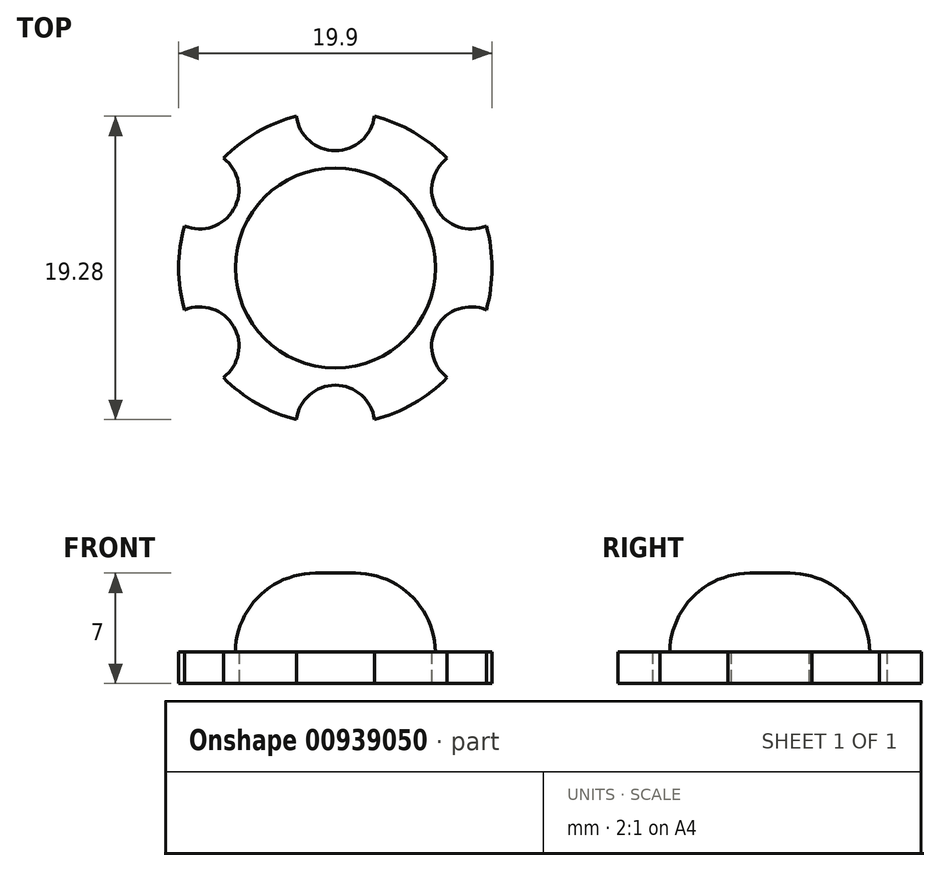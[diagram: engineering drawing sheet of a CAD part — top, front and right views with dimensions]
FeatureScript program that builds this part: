
annotation { "Feature Type Name" : "Feature", "Feature Type Description" : "" }
export const myFeature = defineFeature(function(context is Context, id is Id, definition is map)
    precondition{}
    {
        {
            var Q0;
            Q0=qCreatedBy(makeId("Top.planeOp"),FACE);
            var sketch = newSketch(context, id + "F0", { "sketchPlane" : qUnion([Q0])});
            skCircle(sketch, "E0", {"center": v(0, 0) * mm, "radius": 9.95 * mm});
            skCircle(sketch, "E1", {"center": v(0, 9.95) * mm, "radius": 2.5 * mm});
            skCircle(sketch, "E2.1.0", {"center": v(-8.62, 4.98) * mm, "radius": 2.5 * mm});
            skCircle(sketch, "E2.2.0", {"center": v(-8.62, -4.97) * mm, "radius": 2.5 * mm});
            skCircle(sketch, "E2.3.0", {"center": v(0, -9.95) * mm, "radius": 2.5 * mm});
            skCircle(sketch, "E2.4.0", {"center": v(8.62, -4.98) * mm, "radius": 2.5 * mm});
            skCircle(sketch, "E2.5.0", {"center": v(8.62, 4.98) * mm, "radius": 2.5 * mm});
            skSolve(sketch);
        }
        {
            var Q0;
            {var subQ0=sQuery(id+"F0.wireOp",EDGE,"E2.5.0");var subQ1=sQuery(id+"F0.wireOp",EDGE,"E0");var subQ11=makeQuery(id+"F0.imprint","INTERSECT",VERTEX,{"disambiguationData":[OD(0.0)],"derivedFrom":[subQ1,subQ0]});Q0=makeQuery(id+"F0.imprint","IMPRINT",FACE,{"disambiguationData":[TD([[makeQuery(id+"F0.imprint","IMPRINT",EDGE,{"disambiguationData":[TD([[subQ11,-1.0]])],"derivedFrom":subQ1}),1.0]])]});}
            extrude(context, id + "F1", {"entities" : qUnion([Q0]), "depth" : 2 * mm, "offsetDistance" : 25.4 * mm});
        }
        {
            var Q0;
            Q0=makeQuery(id+"F1.opExtrude","CAP_FACE",FACE,{"disambiguationData":[OSD([sQuery(id+"F0.wireOp",EDGE,"E0"),sQuery(id+"F0.wireOp",EDGE,"E1"),sQuery(id+"F0.wireOp",EDGE,"E2.1.0"),sQuery(id+"F0.wireOp",EDGE,"E2.2.0"),sQuery(id+"F0.wireOp",EDGE,"E2.3.0"),sQuery(id+"F0.wireOp",EDGE,"E2.4.0"),sQuery(id+"F0.wireOp",EDGE,"E2.5.0")])],"isStart":false});
            var sketch = newSketch(context, id + "F2", { "sketchPlane" : qUnion([Q0])});
            skCircle(sketch, "E3", {"center": v(0, 0) * mm, "radius": 6.35 * mm});
            skSolve(sketch);
        }
        {
            var Q0;
            Q0 = qSketchRegion(id + "F2", true);
            extrude(context, id + "F3", {"entities" : qUnion([Q0]), "operationType" : NewBodyOperationType.ADD, "depth" : 5 * mm, "offsetDistance" : 25.4 * mm});
        }
        {
            var Q0;
            Q0=makeQuery(id+"F3.opExtrude","CAP_EDGE",EDGE,{"disambiguationData":[OSD([sQuery(id+"F2.wireOp",EDGE,"E3")])],"isStart":false});
            fillet(context, id + "F4", {"entities" : qUnion([Q0]), "radius" : 5.08 * mm, "tangentPropagation" : true, "allowEdgeOverflow" : false});
        }
    });
